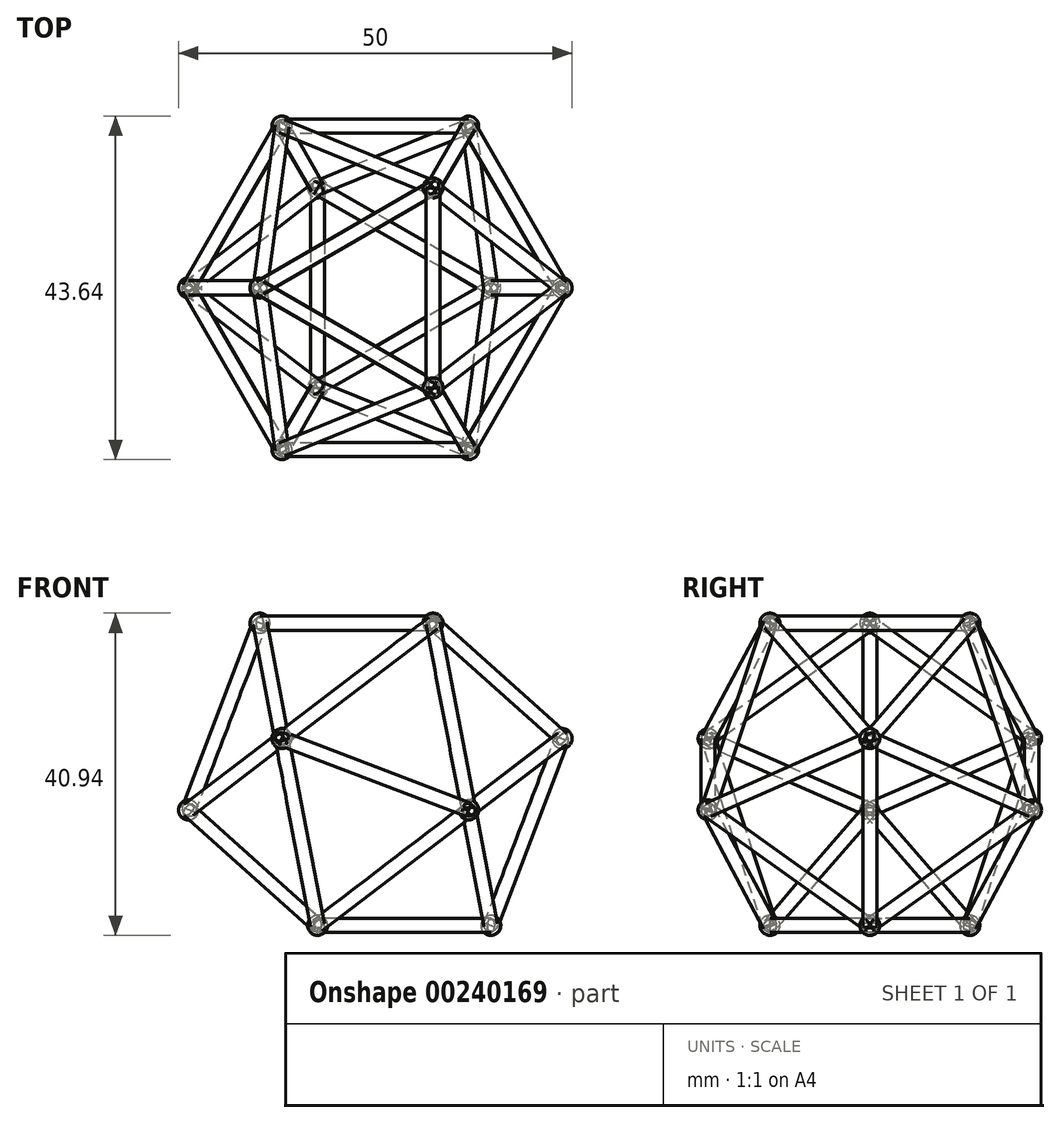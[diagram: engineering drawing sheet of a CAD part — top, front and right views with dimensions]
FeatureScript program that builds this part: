
annotation { "Feature Type Name" : "Feature", "Feature Type Description" : "" }
export const myFeature = defineFeature(function(context is Context, id is Id, definition is map)
    precondition{}
    {
        {
            var Q0;
            Q0=qCreatedBy(makeId("Front.planeOp"),FACE);
            var sketch = newSketch(context, id + "F0", { "sketchPlane" : qUnion([Q0])});
            skLineSegment(sketch, "E0.bottom", {"start": v(-20.55, 12.7) * mm, "end": v(20.55, 12.7) * mm});
            skLineSegment(sketch, "E0.top", {"start": v(-20.55, -12.7) * mm, "end": v(20.55, -12.7) * mm});
            skLineSegment(sketch, "E0.left", {"start": v(-20.55, 12.7) * mm, "end": v(-20.55, -12.7) * mm});
            skLineSegment(sketch, "E0.right", {"start": v(20.55, 12.7) * mm, "end": v(20.55, -12.7) * mm});
            skSolve(sketch);
        }
        {
            var Q0;
            Q0 = qSketchRegion(id + "F0", true);
            extrude(context, id + "F1", {"entities" : qUnion([Q0]), "depth" : 1.27 * mm, "hasSecondDirection" : true, "secondDirectionOppositeDirection" : true, "secondDirectionDepth" : 1.27 * mm});
        }
        {
            var Q0;
            Q0=qCreatedBy(makeId("Top.planeOp"),FACE);
            var sketch = newSketch(context, id + "F2", { "sketchPlane" : qUnion([Q0])});
            skLineSegment(sketch, "E1", {"start": v(0, 0) * mm, "end": v(0, 50.8) * mm});
            skLineSegment(sketch, "E2", {"start": v(0, 0) * mm, "end": v(-50.8, 0) * mm});
            skSolve(sketch);
        }
        {
            var Q0;
            Q0=qCreatedBy(makeId("Front.planeOp"),FACE);
            var sketch = newSketch(context, id + "F3", { "sketchPlane" : qUnion([Q0])});
            skLineSegment(sketch, "E3", {"start": v(0, 0) * mm, "end": v(0, 50.8) * mm});
            skSolve(sketch);
        }
        {
            var Q0;
            Q0=makeQuery(id+"F1.opExtrude","SWEPT_BODY",BODY,{"disambiguationData":[OSD([sQuery(id+"F0.wireOp",EDGE,"E0.bottom"),sQuery(id+"F0.wireOp",EDGE,"E0.top"),sQuery(id+"F0.wireOp",EDGE,"E0.left"),sQuery(id+"F0.wireOp",EDGE,"E0.right")])]});
            var Q1;
            Q1=sQuery(id+"F2.wireOp",EDGE,"E1");
            transform(context, id + "F4", {"entities" : qUnion([Q0]), "transformType" : TransformType.ROTATION, "transformAxis" : qUnion([Q1]), "angle" : 90 * degree, "makeCopy" : true});
        }
        {
            var Q0;
            Q0=makeQuery(id+"F4.opPattern","COPY",BODY,{"derivedFrom":makeQuery(id+"F1.opExtrude","SWEPT_BODY",BODY,{"disambiguationData":[OSD([sQuery(id+"F0.wireOp",EDGE,"E0.bottom"),sQuery(id+"F0.wireOp",EDGE,"E0.top"),sQuery(id+"F0.wireOp",EDGE,"E0.left"),sQuery(id+"F0.wireOp",EDGE,"E0.right")])]}),"instanceName":"1"});
            var Q1;
            Q1=sQuery(id+"F2.wireOp",EDGE,"E2");
            transform(context, id + "F5", {"entities" : qUnion([Q0]), "transformType" : TransformType.ROTATION, "transformAxis" : qUnion([Q1]), "angle" : 90 * degree, "makeCopy" : false});
        }
        {
            var Q0;
            Q0=makeQuery(id+"F1.opExtrude","SWEPT_BODY",BODY,{"disambiguationData":[OSD([sQuery(id+"F0.wireOp",EDGE,"E0.bottom"),sQuery(id+"F0.wireOp",EDGE,"E0.top"),sQuery(id+"F0.wireOp",EDGE,"E0.left"),sQuery(id+"F0.wireOp",EDGE,"E0.right")])]});
            var Q1;
            Q1=sQuery(id+"F3.wireOp",EDGE,"E3");
            transform(context, id + "F6", {"entities" : qUnion([Q0]), "transformType" : TransformType.ROTATION, "transformAxis" : qUnion([Q1]), "angle" : 90 * degree, "makeCopy" : true});
        }
        {
            var Q0;
            Q0=makeQuery(id+"F6.opPattern","COPY",BODY,{"derivedFrom":makeQuery(id+"F1.opExtrude","SWEPT_BODY",BODY,{"disambiguationData":[OSD([sQuery(id+"F0.wireOp",EDGE,"E0.bottom"),sQuery(id+"F0.wireOp",EDGE,"E0.top"),sQuery(id+"F0.wireOp",EDGE,"E0.left"),sQuery(id+"F0.wireOp",EDGE,"E0.right")])]}),"instanceName":"1"});
            var Q1;
            Q1=sQuery(id+"F2.wireOp",EDGE,"E2");
            transform(context, id + "F7", {"entities" : qUnion([Q0]), "transformType" : TransformType.ROTATION, "transformAxis" : qUnion([Q1]), "angle" : 90 * degree, "makeCopy" : false});
        }
        {
            var Q0;
            Q0=makeQuery(id+"F6.opPattern","COPY",FACE,{"derivedFrom":makeQuery(id+"F1.opExtrude","SWEPT_FACE",FACE,{"disambiguationData":[OSD([sQuery(id+"F0.wireOp",EDGE,"E0.left")])]}),"instanceName":"1"});
            var sketch = newSketch(context, id + "F8", { "sketchPlane" : qUnion([Q0])});
            skArc(sketch, "E4", {"start": v(1.27, 12.7) * mm, "mid": v(0, 13.97) * mm, "end": v(-1.27, 12.7) * mm});
            skArc(sketch, "E5", {"start": v(-1.27, -12.7) * mm, "mid": v(0, -13.97) * mm, "end": v(1.27, -12.7) * mm});
            skLineSegment(sketch, "E6", {"start": v(-1.27, 12.7) * mm, "end": v(1.27, 12.7) * mm});
            skLineSegment(sketch, "E7", {"start": v(-1.27, -12.7) * mm, "end": v(1.27, -12.7) * mm});
            skSolve(sketch);
        }
        {
            var Q0;
            Q0=makeQuery(id+"F8.imprint","IMPRINT",FACE,{"disambiguationData":[TD([[makeQuery(id+"F8.imprint","IMPRINT",EDGE,{"derivedFrom":sQuery(id+"F8.wireOp",EDGE,"E4")}),1.0]])]});
            var Q1;
            Q1=sQuery(id+"F8.wireOp",EDGE,"E6");
            revolve(context, id + "F9", {"entities" : qUnion([Q0]), "axis" : qUnion([Q1]), "revolveType" : RevolveType.FULL});
        }
        {
            var Q0;
            Q0=makeQuery(id+"F8.imprint","IMPRINT",FACE,{"disambiguationData":[TD([[makeQuery(id+"F8.imprint","IMPRINT",EDGE,{"derivedFrom":sQuery(id+"F8.wireOp",EDGE,"E5")}),1.0]])]});
            var Q1;
            Q1=sQuery(id+"F8.wireOp",EDGE,"E7");
            revolve(context, id + "F10", {"entities" : qUnion([Q0]), "axis" : qUnion([Q1]), "revolveType" : RevolveType.FULL});
        }
        {
            var Q0;
            Q0=makeQuery(id+"F1.opExtrude","SWEPT_FACE",FACE,{"disambiguationData":[OSD([sQuery(id+"F0.wireOp",EDGE,"E0.right")])]});
            var sketch = newSketch(context, id + "F11", { "sketchPlane" : qUnion([Q0])});
            skArc(sketch, "E8", {"start": v(1.27, 12.7) * mm, "mid": v(0, 13.97) * mm, "end": v(-1.27, 12.7) * mm});
            skArc(sketch, "E9", {"start": v(-1.27, -12.7) * mm, "mid": v(0, -13.97) * mm, "end": v(1.27, -12.7) * mm});
            skLineSegment(sketch, "E10", {"start": v(-1.27, 12.7) * mm, "end": v(1.27, 12.7) * mm});
            skLineSegment(sketch, "E11", {"start": v(-1.27, -12.7) * mm, "end": v(1.27, -12.7) * mm});
            skSolve(sketch);
        }
        {
            var Q0;
            Q0=makeQuery(id+"F11.imprint","IMPRINT",FACE,{"disambiguationData":[TD([[makeQuery(id+"F11.imprint","IMPRINT",EDGE,{"derivedFrom":sQuery(id+"F11.wireOp",EDGE,"E8")}),1.0]])]});
            var Q1;
            Q1=sQuery(id+"F11.wireOp",EDGE,"E10");
            revolve(context, id + "F12", {"entities" : qUnion([Q0]), "axis" : qUnion([Q1]), "revolveType" : RevolveType.FULL});
        }
        {
            var Q0;
            Q0=sQuery(id+"F8.wireOp",EDGE,"E7");
            cPoint(context, id + "F13", {"entities" : qUnion([Q0]), "parameter" : 0.5});
        }
        {
            var Q0;
            Q0=sQuery(id+"F11.wireOp",EDGE,"E10");
            cPoint(context, id + "F14", {"entities" : qUnion([Q0]), "parameter" : 0.5});
        }
        {
            var Q0;
            Q0 = qCreatedBy(id + "F13" ,VERTEX);
            var Q1;
            Q1=sQuery(id+"F8.wireOp",VERTEX,"E4.center");
            var Q2;
            Q2 = qCreatedBy(id + "F14" ,VERTEX);
            cPlane(context, id + "F15", {"entities" : qUnion([Q0, Q1, Q2]), "cplaneType" : CPlaneType.THREE_POINT, "offset" : 25.4 * mm, "width" : 152.4 * mm, "height" : 152.4 * mm});
        }
        {
            var Q0;
            Q0=qCreatedBy(id+"F15.planeOp",FACE);
            var sketch = newSketch(context, id + "F16", { "sketchPlane" : qUnion([Q0])});
            skPoint(sketch, "E12.0", {"position": v(-7.33, 12.7) * mm});
            skPoint(sketch, "E13.0", {"position": v(-7.33, -12.7) * mm});
            skPoint(sketch, "E14.0", {"position": v(14.66, 0) * mm});
            skLineSegment(sketch, "E15", {"start": v(-7.33, 12.7) * mm, "end": v(-7.33, -12.7) * mm});
            skLineSegment(sketch, "E16", {"start": v(-7.33, -12.7) * mm, "end": v(14.66, 0) * mm});
            skLineSegment(sketch, "E17", {"start": v(-7.33, 12.7) * mm, "end": v(14.66, 0) * mm});
            skSolve(sketch);
        }
        {
            var Q0;
            Q0=sQuery(id+"F8.wireOp",EDGE,"E6");
            cPoint(context, id + "F17", {"entities" : qUnion([Q0]), "parameter" : 0.5});
        }
        {
            var Q0;
            Q0 = qCreatedBy(id + "F17" ,VERTEX);
            var Q1;
            Q1=sQuery(id+"F16.wireOp",EDGE,"E17");
            cPlane(context, id + "F18", {"entities" : qUnion([Q0, Q1]), "cplaneType" : CPlaneType.LINE_POINT, "offset" : 25.4 * mm, "width" : 152.4 * mm, "height" : 152.4 * mm});
        }
        {
            var Q0;
            Q0=qCreatedBy(id+"F18.planeOp",FACE);
            var sketch = newSketch(context, id + "F19", { "sketchPlane" : qUnion([Q0])});
            skPoint(sketch, "E18.0", {"position": v(7.33, 19.2) * mm});
            skCircle(sketch, "E19", {"center": v(7.33, 19.2) * mm, "radius": 0.9 * mm});
            skSolve(sketch);
        }
        {
            var Q0;
            Q0 = qSketchRegion(id + "F19", true);
            extrude(context, id + "F20", {"entities" : qUnion([Q0]), "depth" : 25.4 * mm});
        }
        {
            var Q0;
            Q0=sQuery(id+"F8.wireOp",EDGE,"E7");
            cPoint(context, id + "F21", {"entities" : qUnion([Q0]), "parameter" : 0.5});
        }
        {
            var Q0;
            Q0 = qCreatedBy(id + "F21" ,VERTEX);
            var Q1;
            Q1=sQuery(id+"F16.wireOp",EDGE,"E16");
            cPlane(context, id + "F22", {"entities" : qUnion([Q0, Q1]), "cplaneType" : CPlaneType.LINE_POINT, "offset" : 25.4 * mm, "width" : 152.4 * mm, "height" : 152.4 * mm});
        }
        {
            var Q0;
            Q0=qCreatedBy(id+"F22.planeOp",FACE);
            var sketch = newSketch(context, id + "F23", { "sketchPlane" : qUnion([Q0])});
            skPoint(sketch, "E20.0", {"position": v(-7.33, 19.2) * mm});
            skCircle(sketch, "E21", {"center": v(-7.33, 19.2) * mm, "radius": 0.9 * mm});
            skSolve(sketch);
        }
        {
            var Q0;
            Q0 = qSketchRegion(id + "F23", true);
            extrude(context, id + "F24", {"entities" : qUnion([Q0]), "depth" : 25.4 * mm});
        }
        {
            var Q0;
            Q0=makeQuery(id+"F20.opExtrude","SWEPT_BODY",BODY,{"disambiguationData":[OSD([sQuery(id+"F19.wireOp",EDGE,"E19")])]});
            var Q1;
            Q1=makeQuery(id+"F24.opExtrude","SWEPT_BODY",BODY,{"disambiguationData":[OSD([sQuery(id+"F23.wireOp",EDGE,"E21")])]});
            var Q2;
            Q2=makeQuery(id+"F12.opRevolve","SWEPT_BODY",BODY,{"disambiguationData":[OSD([sQuery(id+"F11.wireOp",EDGE,"E8"),sQuery(id+"F11.wireOp",EDGE,"E10")])]});
            var Q3;
            Q3=qCreatedBy(makeId("Right.planeOp"),FACE);
            mirror(context, id + "F25", {"entities" : qUnion([Q0, Q1, Q2]), "mirrorPlane" : qUnion([Q3])});
        }
        {
            var Q0;
            Q0=makeQuery(id+"F25.opPattern","COPY",BODY,{"derivedFrom":makeQuery(id+"F12.opRevolve","SWEPT_BODY",BODY,{"disambiguationData":[OSD([sQuery(id+"F11.wireOp",EDGE,"E8"),sQuery(id+"F11.wireOp",EDGE,"E10")])]}),"instanceName":"1"});
            var Q1;
            Q1=makeQuery(id+"F25.opPattern","COPY",BODY,{"derivedFrom":makeQuery(id+"F20.opExtrude","SWEPT_BODY",BODY,{"disambiguationData":[OSD([sQuery(id+"F19.wireOp",EDGE,"E19")])]}),"instanceName":"1"});
            var Q2;
            Q2=makeQuery(id+"F9.opRevolve","SWEPT_BODY",BODY,{"disambiguationData":[OSD([sQuery(id+"F8.wireOp",EDGE,"E4"),sQuery(id+"F8.wireOp",EDGE,"E6")])]});
            var Q3;
            Q3=makeQuery(id+"F20.opExtrude","SWEPT_BODY",BODY,{"disambiguationData":[OSD([sQuery(id+"F19.wireOp",EDGE,"E19")])]});
            var Q4;
            Q4=makeQuery(id+"F12.opRevolve","SWEPT_BODY",BODY,{"disambiguationData":[OSD([sQuery(id+"F11.wireOp",EDGE,"E8"),sQuery(id+"F11.wireOp",EDGE,"E10")])]});
            var Q5;
            Q5=makeQuery(id+"F10.opRevolve","SWEPT_BODY",BODY,{"disambiguationData":[OSD([sQuery(id+"F8.wireOp",EDGE,"E5"),sQuery(id+"F8.wireOp",EDGE,"E7")])]});
            var Q6;
            Q6=makeQuery(id+"F25.opPattern","COPY",BODY,{"derivedFrom":makeQuery(id+"F24.opExtrude","SWEPT_BODY",BODY,{"disambiguationData":[OSD([sQuery(id+"F23.wireOp",EDGE,"E21")])]}),"instanceName":"1"});
            var Q7;
            Q7=makeQuery(id+"F24.opExtrude","SWEPT_BODY",BODY,{"disambiguationData":[OSD([sQuery(id+"F23.wireOp",EDGE,"E21")])]});
            var Q8;
            Q8=qCreatedBy(makeId("Top.planeOp"),FACE);
            mirror(context, id + "F26", {"entities" : qUnion([Q0, Q1, Q2, Q3, Q4, Q5, Q6, Q7]), "mirrorPlane" : qUnion([Q8])});
        }
        {
            var Q0;
            Q0=makeQuery(id+"F6.opPattern","COPY",FACE,{"derivedFrom":makeQuery(id+"F1.opExtrude","SWEPT_FACE",FACE,{"disambiguationData":[OSD([sQuery(id+"F0.wireOp",EDGE,"E0.top")])]}),"instanceName":"1"});
            var sketch = newSketch(context, id + "F27", { "sketchPlane" : qUnion([Q0])});
            skPoint(sketch, "E22.0", {"position": v(0, 20.55) * mm});
            skCircle(sketch, "E23", {"center": v(0, 20.55) * mm, "radius": 0.9 * mm});
            skSolve(sketch);
        }
        {
            var Q0;
            Q0 = qSketchRegion(id + "F27", true);
            extrude(context, id + "F28", {"entities" : qUnion([Q0]), "oppositeDirection" : true, "depth" : 25.4 * mm});
        }
        {
            var Q0;
            Q0=makeQuery(id+"F28.opExtrude","SWEPT_BODY",BODY,{"disambiguationData":[OSD([sQuery(id+"F27.wireOp",EDGE,"E23")])]});
            var Q1;
            Q1=qCreatedBy(makeId("Top.planeOp"),FACE);
            mirror(context, id + "F29", {"entities" : qUnion([Q0]), "mirrorPlane" : qUnion([Q1])});
        }
        {
            var Q0;
            Q0=makeQuery(id+"F1.opExtrude","SWEPT_BODY",BODY,{"disambiguationData":[OSD([sQuery(id+"F0.wireOp",EDGE,"E0.bottom"),sQuery(id+"F0.wireOp",EDGE,"E0.top"),sQuery(id+"F0.wireOp",EDGE,"E0.left"),sQuery(id+"F0.wireOp",EDGE,"E0.right")])]});
            deleteBodies(context, id + "F30", {"entities" : qUnion([Q0])});
        }
        {
            var Q0;
            Q0=makeQuery(id+"F4.opPattern","COPY",BODY,{"derivedFrom":makeQuery(id+"F1.opExtrude","SWEPT_BODY",BODY,{"disambiguationData":[OSD([sQuery(id+"F0.wireOp",EDGE,"E0.bottom"),sQuery(id+"F0.wireOp",EDGE,"E0.top"),sQuery(id+"F0.wireOp",EDGE,"E0.left"),sQuery(id+"F0.wireOp",EDGE,"E0.right")])]}),"instanceName":"1"});
            deleteBodies(context, id + "F31", {"entities" : qUnion([Q0])});
        }
        {
            var Q0;
            Q0=makeQuery(id+"F6.opPattern","COPY",BODY,{"derivedFrom":makeQuery(id+"F1.opExtrude","SWEPT_BODY",BODY,{"disambiguationData":[OSD([sQuery(id+"F0.wireOp",EDGE,"E0.bottom"),sQuery(id+"F0.wireOp",EDGE,"E0.top"),sQuery(id+"F0.wireOp",EDGE,"E0.left"),sQuery(id+"F0.wireOp",EDGE,"E0.right")])]}),"instanceName":"1"});
            var Q1;
            Q1=makeQuery(id+"F9.opRevolve","SWEPT_BODY",BODY,{"disambiguationData":[OSD([sQuery(id+"F8.wireOp",EDGE,"E4"),sQuery(id+"F8.wireOp",EDGE,"E6")])]});
            var Q2;
            Q2=makeQuery(id+"F10.opRevolve","SWEPT_BODY",BODY,{"disambiguationData":[OSD([sQuery(id+"F8.wireOp",EDGE,"E5"),sQuery(id+"F8.wireOp",EDGE,"E7")])]});
            var Q3;
            Q3=makeQuery(id+"F12.opRevolve","SWEPT_BODY",BODY,{"disambiguationData":[OSD([sQuery(id+"F11.wireOp",EDGE,"E8"),sQuery(id+"F11.wireOp",EDGE,"E10")])]});
            var Q4;
            Q4=makeQuery(id+"F20.opExtrude","SWEPT_BODY",BODY,{"disambiguationData":[OSD([sQuery(id+"F19.wireOp",EDGE,"E19")])]});
            var Q5;
            Q5=makeQuery(id+"F24.opExtrude","SWEPT_BODY",BODY,{"disambiguationData":[OSD([sQuery(id+"F23.wireOp",EDGE,"E21")])]});
            var Q6;
            Q6=makeQuery(id+"F25.opPattern","COPY",BODY,{"derivedFrom":makeQuery(id+"F12.opRevolve","SWEPT_BODY",BODY,{"disambiguationData":[OSD([sQuery(id+"F11.wireOp",EDGE,"E8"),sQuery(id+"F11.wireOp",EDGE,"E10")])]}),"instanceName":"1"});
            var Q7;
            Q7=makeQuery(id+"F25.opPattern","COPY",BODY,{"derivedFrom":makeQuery(id+"F20.opExtrude","SWEPT_BODY",BODY,{"disambiguationData":[OSD([sQuery(id+"F19.wireOp",EDGE,"E19")])]}),"instanceName":"1"});
            var Q8;
            Q8=makeQuery(id+"F25.opPattern","COPY",BODY,{"derivedFrom":makeQuery(id+"F24.opExtrude","SWEPT_BODY",BODY,{"disambiguationData":[OSD([sQuery(id+"F23.wireOp",EDGE,"E21")])]}),"instanceName":"1"});
            var Q9;
            Q9=makeQuery(id+"F26.opPattern","COPY",BODY,{"derivedFrom":makeQuery(id+"F9.opRevolve","SWEPT_BODY",BODY,{"disambiguationData":[OSD([sQuery(id+"F8.wireOp",EDGE,"E4"),sQuery(id+"F8.wireOp",EDGE,"E6")])]}),"instanceName":"1"});
            var Q10;
            Q10=makeQuery(id+"F26.opPattern","COPY",BODY,{"derivedFrom":makeQuery(id+"F10.opRevolve","SWEPT_BODY",BODY,{"disambiguationData":[OSD([sQuery(id+"F8.wireOp",EDGE,"E5"),sQuery(id+"F8.wireOp",EDGE,"E7")])]}),"instanceName":"1"});
            var Q11;
            Q11=makeQuery(id+"F26.opPattern","COPY",BODY,{"derivedFrom":makeQuery(id+"F12.opRevolve","SWEPT_BODY",BODY,{"disambiguationData":[OSD([sQuery(id+"F11.wireOp",EDGE,"E8"),sQuery(id+"F11.wireOp",EDGE,"E10")])]}),"instanceName":"1"});
            var Q12;
            Q12=makeQuery(id+"F26.opPattern","COPY",BODY,{"derivedFrom":makeQuery(id+"F20.opExtrude","SWEPT_BODY",BODY,{"disambiguationData":[OSD([sQuery(id+"F19.wireOp",EDGE,"E19")])]}),"instanceName":"1"});
            var Q13;
            Q13=makeQuery(id+"F26.opPattern","COPY",BODY,{"derivedFrom":makeQuery(id+"F24.opExtrude","SWEPT_BODY",BODY,{"disambiguationData":[OSD([sQuery(id+"F23.wireOp",EDGE,"E21")])]}),"instanceName":"1"});
            var Q14;
            Q14=makeQuery(id+"F26.opPattern","COPY",BODY,{"derivedFrom":makeQuery(id+"F25.opPattern","COPY",BODY,{"derivedFrom":makeQuery(id+"F12.opRevolve","SWEPT_BODY",BODY,{"disambiguationData":[OSD([sQuery(id+"F11.wireOp",EDGE,"E8"),sQuery(id+"F11.wireOp",EDGE,"E10")])]}),"instanceName":"1"}),"instanceName":"1"});
            var Q15;
            Q15=makeQuery(id+"F26.opPattern","COPY",BODY,{"derivedFrom":makeQuery(id+"F25.opPattern","COPY",BODY,{"derivedFrom":makeQuery(id+"F20.opExtrude","SWEPT_BODY",BODY,{"disambiguationData":[OSD([sQuery(id+"F19.wireOp",EDGE,"E19")])]}),"instanceName":"1"}),"instanceName":"1"});
            var Q16;
            Q16=makeQuery(id+"F26.opPattern","COPY",BODY,{"derivedFrom":makeQuery(id+"F25.opPattern","COPY",BODY,{"derivedFrom":makeQuery(id+"F24.opExtrude","SWEPT_BODY",BODY,{"disambiguationData":[OSD([sQuery(id+"F23.wireOp",EDGE,"E21")])]}),"instanceName":"1"}),"instanceName":"1"});
            var Q17;
            Q17=makeQuery(id+"F28.opExtrude","SWEPT_BODY",BODY,{"disambiguationData":[OSD([sQuery(id+"F27.wireOp",EDGE,"E23")])]});
            var Q18;
            Q18=makeQuery(id+"F29.opPattern","COPY",BODY,{"derivedFrom":makeQuery(id+"F28.opExtrude","SWEPT_BODY",BODY,{"disambiguationData":[OSD([sQuery(id+"F27.wireOp",EDGE,"E23")])]}),"instanceName":"1"});
            var Q19;
            Q19=sQuery(id+"F2.wireOp",EDGE,"E1");
            transform(context, id + "F32", {"entities" : qUnion([Q0, Q1, Q2, Q3, Q4, Q5, Q6, Q7, Q8, Q9, Q10, Q11, Q12, Q13, Q14, Q15, Q16, Q17, Q18]), "transformType" : TransformType.ROTATION, "transformAxis" : qUnion([Q19]), "angle" : 90 * degree, "makeCopy" : true});
        }
        {
            var Q0;
            Q0=makeQuery(id+"F32.opPattern","COPY",BODY,{"derivedFrom":makeQuery(id+"F6.opPattern","COPY",BODY,{"derivedFrom":makeQuery(id+"F1.opExtrude","SWEPT_BODY",BODY,{"disambiguationData":[OSD([sQuery(id+"F0.wireOp",EDGE,"E0.bottom"),sQuery(id+"F0.wireOp",EDGE,"E0.top"),sQuery(id+"F0.wireOp",EDGE,"E0.left"),sQuery(id+"F0.wireOp",EDGE,"E0.right")])]}),"instanceName":"1"}),"instanceName":"1"});
            var Q1;
            Q1=makeQuery(id+"F32.opPattern","COPY",BODY,{"derivedFrom":makeQuery(id+"F9.opRevolve","SWEPT_BODY",BODY,{"disambiguationData":[OSD([sQuery(id+"F8.wireOp",EDGE,"E4"),sQuery(id+"F8.wireOp",EDGE,"E6")])]}),"instanceName":"1"});
            var Q2;
            Q2=makeQuery(id+"F32.opPattern","COPY",BODY,{"derivedFrom":makeQuery(id+"F10.opRevolve","SWEPT_BODY",BODY,{"disambiguationData":[OSD([sQuery(id+"F8.wireOp",EDGE,"E5"),sQuery(id+"F8.wireOp",EDGE,"E7")])]}),"instanceName":"1"});
            var Q3;
            Q3=makeQuery(id+"F32.opPattern","COPY",BODY,{"derivedFrom":makeQuery(id+"F12.opRevolve","SWEPT_BODY",BODY,{"disambiguationData":[OSD([sQuery(id+"F11.wireOp",EDGE,"E8"),sQuery(id+"F11.wireOp",EDGE,"E10")])]}),"instanceName":"1"});
            var Q4;
            Q4=makeQuery(id+"F32.opPattern","COPY",BODY,{"derivedFrom":makeQuery(id+"F20.opExtrude","SWEPT_BODY",BODY,{"disambiguationData":[OSD([sQuery(id+"F19.wireOp",EDGE,"E19")])]}),"instanceName":"1"});
            var Q5;
            Q5=makeQuery(id+"F32.opPattern","COPY",BODY,{"derivedFrom":makeQuery(id+"F24.opExtrude","SWEPT_BODY",BODY,{"disambiguationData":[OSD([sQuery(id+"F23.wireOp",EDGE,"E21")])]}),"instanceName":"1"});
            var Q6;
            Q6=makeQuery(id+"F32.opPattern","COPY",BODY,{"derivedFrom":makeQuery(id+"F25.opPattern","COPY",BODY,{"derivedFrom":makeQuery(id+"F12.opRevolve","SWEPT_BODY",BODY,{"disambiguationData":[OSD([sQuery(id+"F11.wireOp",EDGE,"E8"),sQuery(id+"F11.wireOp",EDGE,"E10")])]}),"instanceName":"1"}),"instanceName":"1"});
            var Q7;
            Q7=makeQuery(id+"F32.opPattern","COPY",BODY,{"derivedFrom":makeQuery(id+"F25.opPattern","COPY",BODY,{"derivedFrom":makeQuery(id+"F20.opExtrude","SWEPT_BODY",BODY,{"disambiguationData":[OSD([sQuery(id+"F19.wireOp",EDGE,"E19")])]}),"instanceName":"1"}),"instanceName":"1"});
            var Q8;
            Q8=makeQuery(id+"F32.opPattern","COPY",BODY,{"derivedFrom":makeQuery(id+"F25.opPattern","COPY",BODY,{"derivedFrom":makeQuery(id+"F24.opExtrude","SWEPT_BODY",BODY,{"disambiguationData":[OSD([sQuery(id+"F23.wireOp",EDGE,"E21")])]}),"instanceName":"1"}),"instanceName":"1"});
            var Q9;
            Q9=makeQuery(id+"F32.opPattern","COPY",BODY,{"derivedFrom":makeQuery(id+"F26.opPattern","COPY",BODY,{"derivedFrom":makeQuery(id+"F9.opRevolve","SWEPT_BODY",BODY,{"disambiguationData":[OSD([sQuery(id+"F8.wireOp",EDGE,"E4"),sQuery(id+"F8.wireOp",EDGE,"E6")])]}),"instanceName":"1"}),"instanceName":"1"});
            var Q10;
            Q10=makeQuery(id+"F32.opPattern","COPY",BODY,{"derivedFrom":makeQuery(id+"F26.opPattern","COPY",BODY,{"derivedFrom":makeQuery(id+"F10.opRevolve","SWEPT_BODY",BODY,{"disambiguationData":[OSD([sQuery(id+"F8.wireOp",EDGE,"E5"),sQuery(id+"F8.wireOp",EDGE,"E7")])]}),"instanceName":"1"}),"instanceName":"1"});
            var Q11;
            Q11=makeQuery(id+"F32.opPattern","COPY",BODY,{"derivedFrom":makeQuery(id+"F26.opPattern","COPY",BODY,{"derivedFrom":makeQuery(id+"F12.opRevolve","SWEPT_BODY",BODY,{"disambiguationData":[OSD([sQuery(id+"F11.wireOp",EDGE,"E8"),sQuery(id+"F11.wireOp",EDGE,"E10")])]}),"instanceName":"1"}),"instanceName":"1"});
            var Q12;
            Q12=makeQuery(id+"F32.opPattern","COPY",BODY,{"derivedFrom":makeQuery(id+"F26.opPattern","COPY",BODY,{"derivedFrom":makeQuery(id+"F20.opExtrude","SWEPT_BODY",BODY,{"disambiguationData":[OSD([sQuery(id+"F19.wireOp",EDGE,"E19")])]}),"instanceName":"1"}),"instanceName":"1"});
            var Q13;
            Q13=makeQuery(id+"F32.opPattern","COPY",BODY,{"derivedFrom":makeQuery(id+"F26.opPattern","COPY",BODY,{"derivedFrom":makeQuery(id+"F24.opExtrude","SWEPT_BODY",BODY,{"disambiguationData":[OSD([sQuery(id+"F23.wireOp",EDGE,"E21")])]}),"instanceName":"1"}),"instanceName":"1"});
            var Q14;
            Q14=makeQuery(id+"F32.opPattern","COPY",BODY,{"derivedFrom":makeQuery(id+"F26.opPattern","COPY",BODY,{"derivedFrom":makeQuery(id+"F25.opPattern","COPY",BODY,{"derivedFrom":makeQuery(id+"F12.opRevolve","SWEPT_BODY",BODY,{"disambiguationData":[OSD([sQuery(id+"F11.wireOp",EDGE,"E8"),sQuery(id+"F11.wireOp",EDGE,"E10")])]}),"instanceName":"1"}),"instanceName":"1"}),"instanceName":"1"});
            var Q15;
            Q15=makeQuery(id+"F32.opPattern","COPY",BODY,{"derivedFrom":makeQuery(id+"F26.opPattern","COPY",BODY,{"derivedFrom":makeQuery(id+"F25.opPattern","COPY",BODY,{"derivedFrom":makeQuery(id+"F20.opExtrude","SWEPT_BODY",BODY,{"disambiguationData":[OSD([sQuery(id+"F19.wireOp",EDGE,"E19")])]}),"instanceName":"1"}),"instanceName":"1"}),"instanceName":"1"});
            var Q16;
            Q16=makeQuery(id+"F32.opPattern","COPY",BODY,{"derivedFrom":makeQuery(id+"F26.opPattern","COPY",BODY,{"derivedFrom":makeQuery(id+"F25.opPattern","COPY",BODY,{"derivedFrom":makeQuery(id+"F24.opExtrude","SWEPT_BODY",BODY,{"disambiguationData":[OSD([sQuery(id+"F23.wireOp",EDGE,"E21")])]}),"instanceName":"1"}),"instanceName":"1"}),"instanceName":"1"});
            var Q17;
            Q17=makeQuery(id+"F32.opPattern","COPY",BODY,{"derivedFrom":makeQuery(id+"F28.opExtrude","SWEPT_BODY",BODY,{"disambiguationData":[OSD([sQuery(id+"F27.wireOp",EDGE,"E23")])]}),"instanceName":"1"});
            var Q18;
            Q18=makeQuery(id+"F32.opPattern","COPY",BODY,{"derivedFrom":makeQuery(id+"F29.opPattern","COPY",BODY,{"derivedFrom":makeQuery(id+"F28.opExtrude","SWEPT_BODY",BODY,{"disambiguationData":[OSD([sQuery(id+"F27.wireOp",EDGE,"E23")])]}),"instanceName":"1"}),"instanceName":"1"});
            var Q19;
            Q19=sQuery(id+"F3.wireOp",EDGE,"E3");
            transform(context, id + "F33", {"entities" : qUnion([Q0, Q1, Q2, Q3, Q4, Q5, Q6, Q7, Q8, Q9, Q10, Q11, Q12, Q13, Q14, Q15, Q16, Q17, Q18]), "transformType" : TransformType.ROTATION, "transformAxis" : qUnion([Q19]), "angle" : 90 * degree, "makeCopy" : false});
        }
        {
            var Q0;
            Q0=makeQuery(id+"F6.opPattern","COPY",BODY,{"derivedFrom":makeQuery(id+"F1.opExtrude","SWEPT_BODY",BODY,{"disambiguationData":[OSD([sQuery(id+"F0.wireOp",EDGE,"E0.bottom"),sQuery(id+"F0.wireOp",EDGE,"E0.top"),sQuery(id+"F0.wireOp",EDGE,"E0.left"),sQuery(id+"F0.wireOp",EDGE,"E0.right")])]}),"instanceName":"1"});
            var Q1;
            Q1=makeQuery(id+"F9.opRevolve","SWEPT_BODY",BODY,{"disambiguationData":[OSD([sQuery(id+"F8.wireOp",EDGE,"E4"),sQuery(id+"F8.wireOp",EDGE,"E6")])]});
            var Q2;
            Q2=makeQuery(id+"F10.opRevolve","SWEPT_BODY",BODY,{"disambiguationData":[OSD([sQuery(id+"F8.wireOp",EDGE,"E5"),sQuery(id+"F8.wireOp",EDGE,"E7")])]});
            var Q3;
            Q3=makeQuery(id+"F12.opRevolve","SWEPT_BODY",BODY,{"disambiguationData":[OSD([sQuery(id+"F11.wireOp",EDGE,"E8"),sQuery(id+"F11.wireOp",EDGE,"E10")])]});
            var Q4;
            Q4=makeQuery(id+"F20.opExtrude","SWEPT_BODY",BODY,{"disambiguationData":[OSD([sQuery(id+"F19.wireOp",EDGE,"E19")])]});
            var Q5;
            Q5=makeQuery(id+"F24.opExtrude","SWEPT_BODY",BODY,{"disambiguationData":[OSD([sQuery(id+"F23.wireOp",EDGE,"E21")])]});
            var Q6;
            Q6=makeQuery(id+"F25.opPattern","COPY",BODY,{"derivedFrom":makeQuery(id+"F12.opRevolve","SWEPT_BODY",BODY,{"disambiguationData":[OSD([sQuery(id+"F11.wireOp",EDGE,"E8"),sQuery(id+"F11.wireOp",EDGE,"E10")])]}),"instanceName":"1"});
            var Q7;
            Q7=makeQuery(id+"F25.opPattern","COPY",BODY,{"derivedFrom":makeQuery(id+"F20.opExtrude","SWEPT_BODY",BODY,{"disambiguationData":[OSD([sQuery(id+"F19.wireOp",EDGE,"E19")])]}),"instanceName":"1"});
            var Q8;
            Q8=makeQuery(id+"F25.opPattern","COPY",BODY,{"derivedFrom":makeQuery(id+"F24.opExtrude","SWEPT_BODY",BODY,{"disambiguationData":[OSD([sQuery(id+"F23.wireOp",EDGE,"E21")])]}),"instanceName":"1"});
            var Q9;
            Q9=makeQuery(id+"F26.opPattern","COPY",BODY,{"derivedFrom":makeQuery(id+"F9.opRevolve","SWEPT_BODY",BODY,{"disambiguationData":[OSD([sQuery(id+"F8.wireOp",EDGE,"E4"),sQuery(id+"F8.wireOp",EDGE,"E6")])]}),"instanceName":"1"});
            var Q10;
            Q10=makeQuery(id+"F26.opPattern","COPY",BODY,{"derivedFrom":makeQuery(id+"F10.opRevolve","SWEPT_BODY",BODY,{"disambiguationData":[OSD([sQuery(id+"F8.wireOp",EDGE,"E5"),sQuery(id+"F8.wireOp",EDGE,"E7")])]}),"instanceName":"1"});
            var Q11;
            Q11=makeQuery(id+"F26.opPattern","COPY",BODY,{"derivedFrom":makeQuery(id+"F12.opRevolve","SWEPT_BODY",BODY,{"disambiguationData":[OSD([sQuery(id+"F11.wireOp",EDGE,"E8"),sQuery(id+"F11.wireOp",EDGE,"E10")])]}),"instanceName":"1"});
            var Q12;
            Q12=makeQuery(id+"F26.opPattern","COPY",BODY,{"derivedFrom":makeQuery(id+"F20.opExtrude","SWEPT_BODY",BODY,{"disambiguationData":[OSD([sQuery(id+"F19.wireOp",EDGE,"E19")])]}),"instanceName":"1"});
            var Q13;
            Q13=makeQuery(id+"F26.opPattern","COPY",BODY,{"derivedFrom":makeQuery(id+"F24.opExtrude","SWEPT_BODY",BODY,{"disambiguationData":[OSD([sQuery(id+"F23.wireOp",EDGE,"E21")])]}),"instanceName":"1"});
            var Q14;
            Q14=makeQuery(id+"F26.opPattern","COPY",BODY,{"derivedFrom":makeQuery(id+"F25.opPattern","COPY",BODY,{"derivedFrom":makeQuery(id+"F12.opRevolve","SWEPT_BODY",BODY,{"disambiguationData":[OSD([sQuery(id+"F11.wireOp",EDGE,"E8"),sQuery(id+"F11.wireOp",EDGE,"E10")])]}),"instanceName":"1"}),"instanceName":"1"});
            var Q15;
            Q15=makeQuery(id+"F26.opPattern","COPY",BODY,{"derivedFrom":makeQuery(id+"F25.opPattern","COPY",BODY,{"derivedFrom":makeQuery(id+"F20.opExtrude","SWEPT_BODY",BODY,{"disambiguationData":[OSD([sQuery(id+"F19.wireOp",EDGE,"E19")])]}),"instanceName":"1"}),"instanceName":"1"});
            var Q16;
            Q16=makeQuery(id+"F26.opPattern","COPY",BODY,{"derivedFrom":makeQuery(id+"F25.opPattern","COPY",BODY,{"derivedFrom":makeQuery(id+"F24.opExtrude","SWEPT_BODY",BODY,{"disambiguationData":[OSD([sQuery(id+"F23.wireOp",EDGE,"E21")])]}),"instanceName":"1"}),"instanceName":"1"});
            var Q17;
            Q17=makeQuery(id+"F28.opExtrude","SWEPT_BODY",BODY,{"disambiguationData":[OSD([sQuery(id+"F27.wireOp",EDGE,"E23")])]});
            var Q18;
            Q18=makeQuery(id+"F29.opPattern","COPY",BODY,{"derivedFrom":makeQuery(id+"F28.opExtrude","SWEPT_BODY",BODY,{"disambiguationData":[OSD([sQuery(id+"F27.wireOp",EDGE,"E23")])]}),"instanceName":"1"});
            var Q19;
            Q19=sQuery(id+"F2.wireOp",EDGE,"E1");
            transform(context, id + "F34", {"entities" : qUnion([Q0, Q1, Q2, Q3, Q4, Q5, Q6, Q7, Q8, Q9, Q10, Q11, Q12, Q13, Q14, Q15, Q16, Q17, Q18]), "transformType" : TransformType.ROTATION, "transformAxis" : qUnion([Q19]), "angle" : 90 * degree, "makeCopy" : true});
        }
        {
            var Q0;
            Q0=makeQuery(id+"F34.opPattern","COPY",BODY,{"derivedFrom":makeQuery(id+"F6.opPattern","COPY",BODY,{"derivedFrom":makeQuery(id+"F1.opExtrude","SWEPT_BODY",BODY,{"disambiguationData":[OSD([sQuery(id+"F0.wireOp",EDGE,"E0.bottom"),sQuery(id+"F0.wireOp",EDGE,"E0.top"),sQuery(id+"F0.wireOp",EDGE,"E0.left"),sQuery(id+"F0.wireOp",EDGE,"E0.right")])]}),"instanceName":"1"}),"instanceName":"1"});
            var Q1;
            Q1=makeQuery(id+"F34.opPattern","COPY",BODY,{"derivedFrom":makeQuery(id+"F9.opRevolve","SWEPT_BODY",BODY,{"disambiguationData":[OSD([sQuery(id+"F8.wireOp",EDGE,"E4"),sQuery(id+"F8.wireOp",EDGE,"E6")])]}),"instanceName":"1"});
            var Q2;
            Q2=makeQuery(id+"F34.opPattern","COPY",BODY,{"derivedFrom":makeQuery(id+"F10.opRevolve","SWEPT_BODY",BODY,{"disambiguationData":[OSD([sQuery(id+"F8.wireOp",EDGE,"E5"),sQuery(id+"F8.wireOp",EDGE,"E7")])]}),"instanceName":"1"});
            var Q3;
            Q3=makeQuery(id+"F34.opPattern","COPY",BODY,{"derivedFrom":makeQuery(id+"F12.opRevolve","SWEPT_BODY",BODY,{"disambiguationData":[OSD([sQuery(id+"F11.wireOp",EDGE,"E8"),sQuery(id+"F11.wireOp",EDGE,"E10")])]}),"instanceName":"1"});
            var Q4;
            Q4=makeQuery(id+"F34.opPattern","COPY",BODY,{"derivedFrom":makeQuery(id+"F20.opExtrude","SWEPT_BODY",BODY,{"disambiguationData":[OSD([sQuery(id+"F19.wireOp",EDGE,"E19")])]}),"instanceName":"1"});
            var Q5;
            Q5=makeQuery(id+"F34.opPattern","COPY",BODY,{"derivedFrom":makeQuery(id+"F24.opExtrude","SWEPT_BODY",BODY,{"disambiguationData":[OSD([sQuery(id+"F23.wireOp",EDGE,"E21")])]}),"instanceName":"1"});
            var Q6;
            Q6=makeQuery(id+"F34.opPattern","COPY",BODY,{"derivedFrom":makeQuery(id+"F25.opPattern","COPY",BODY,{"derivedFrom":makeQuery(id+"F12.opRevolve","SWEPT_BODY",BODY,{"disambiguationData":[OSD([sQuery(id+"F11.wireOp",EDGE,"E8"),sQuery(id+"F11.wireOp",EDGE,"E10")])]}),"instanceName":"1"}),"instanceName":"1"});
            var Q7;
            Q7=makeQuery(id+"F34.opPattern","COPY",BODY,{"derivedFrom":makeQuery(id+"F25.opPattern","COPY",BODY,{"derivedFrom":makeQuery(id+"F20.opExtrude","SWEPT_BODY",BODY,{"disambiguationData":[OSD([sQuery(id+"F19.wireOp",EDGE,"E19")])]}),"instanceName":"1"}),"instanceName":"1"});
            var Q8;
            Q8=makeQuery(id+"F34.opPattern","COPY",BODY,{"derivedFrom":makeQuery(id+"F25.opPattern","COPY",BODY,{"derivedFrom":makeQuery(id+"F24.opExtrude","SWEPT_BODY",BODY,{"disambiguationData":[OSD([sQuery(id+"F23.wireOp",EDGE,"E21")])]}),"instanceName":"1"}),"instanceName":"1"});
            var Q9;
            Q9=makeQuery(id+"F34.opPattern","COPY",BODY,{"derivedFrom":makeQuery(id+"F26.opPattern","COPY",BODY,{"derivedFrom":makeQuery(id+"F9.opRevolve","SWEPT_BODY",BODY,{"disambiguationData":[OSD([sQuery(id+"F8.wireOp",EDGE,"E4"),sQuery(id+"F8.wireOp",EDGE,"E6")])]}),"instanceName":"1"}),"instanceName":"1"});
            var Q10;
            Q10=makeQuery(id+"F34.opPattern","COPY",BODY,{"derivedFrom":makeQuery(id+"F26.opPattern","COPY",BODY,{"derivedFrom":makeQuery(id+"F10.opRevolve","SWEPT_BODY",BODY,{"disambiguationData":[OSD([sQuery(id+"F8.wireOp",EDGE,"E5"),sQuery(id+"F8.wireOp",EDGE,"E7")])]}),"instanceName":"1"}),"instanceName":"1"});
            var Q11;
            Q11=makeQuery(id+"F34.opPattern","COPY",BODY,{"derivedFrom":makeQuery(id+"F26.opPattern","COPY",BODY,{"derivedFrom":makeQuery(id+"F12.opRevolve","SWEPT_BODY",BODY,{"disambiguationData":[OSD([sQuery(id+"F11.wireOp",EDGE,"E8"),sQuery(id+"F11.wireOp",EDGE,"E10")])]}),"instanceName":"1"}),"instanceName":"1"});
            var Q12;
            Q12=makeQuery(id+"F34.opPattern","COPY",BODY,{"derivedFrom":makeQuery(id+"F26.opPattern","COPY",BODY,{"derivedFrom":makeQuery(id+"F20.opExtrude","SWEPT_BODY",BODY,{"disambiguationData":[OSD([sQuery(id+"F19.wireOp",EDGE,"E19")])]}),"instanceName":"1"}),"instanceName":"1"});
            var Q13;
            Q13=makeQuery(id+"F34.opPattern","COPY",BODY,{"derivedFrom":makeQuery(id+"F26.opPattern","COPY",BODY,{"derivedFrom":makeQuery(id+"F24.opExtrude","SWEPT_BODY",BODY,{"disambiguationData":[OSD([sQuery(id+"F23.wireOp",EDGE,"E21")])]}),"instanceName":"1"}),"instanceName":"1"});
            var Q14;
            Q14=makeQuery(id+"F34.opPattern","COPY",BODY,{"derivedFrom":makeQuery(id+"F26.opPattern","COPY",BODY,{"derivedFrom":makeQuery(id+"F25.opPattern","COPY",BODY,{"derivedFrom":makeQuery(id+"F12.opRevolve","SWEPT_BODY",BODY,{"disambiguationData":[OSD([sQuery(id+"F11.wireOp",EDGE,"E8"),sQuery(id+"F11.wireOp",EDGE,"E10")])]}),"instanceName":"1"}),"instanceName":"1"}),"instanceName":"1"});
            var Q15;
            Q15=makeQuery(id+"F34.opPattern","COPY",BODY,{"derivedFrom":makeQuery(id+"F26.opPattern","COPY",BODY,{"derivedFrom":makeQuery(id+"F25.opPattern","COPY",BODY,{"derivedFrom":makeQuery(id+"F20.opExtrude","SWEPT_BODY",BODY,{"disambiguationData":[OSD([sQuery(id+"F19.wireOp",EDGE,"E19")])]}),"instanceName":"1"}),"instanceName":"1"}),"instanceName":"1"});
            var Q16;
            Q16=makeQuery(id+"F34.opPattern","COPY",BODY,{"derivedFrom":makeQuery(id+"F26.opPattern","COPY",BODY,{"derivedFrom":makeQuery(id+"F25.opPattern","COPY",BODY,{"derivedFrom":makeQuery(id+"F24.opExtrude","SWEPT_BODY",BODY,{"disambiguationData":[OSD([sQuery(id+"F23.wireOp",EDGE,"E21")])]}),"instanceName":"1"}),"instanceName":"1"}),"instanceName":"1"});
            var Q17;
            Q17=makeQuery(id+"F34.opPattern","COPY",BODY,{"derivedFrom":makeQuery(id+"F28.opExtrude","SWEPT_BODY",BODY,{"disambiguationData":[OSD([sQuery(id+"F27.wireOp",EDGE,"E23")])]}),"instanceName":"1"});
            var Q18;
            Q18=makeQuery(id+"F34.opPattern","COPY",BODY,{"derivedFrom":makeQuery(id+"F29.opPattern","COPY",BODY,{"derivedFrom":makeQuery(id+"F28.opExtrude","SWEPT_BODY",BODY,{"disambiguationData":[OSD([sQuery(id+"F27.wireOp",EDGE,"E23")])]}),"instanceName":"1"}),"instanceName":"1"});
            var Q19;
            Q19=sQuery(id+"F2.wireOp",EDGE,"E2");
            transform(context, id + "F35", {"entities" : qUnion([Q0, Q1, Q2, Q3, Q4, Q5, Q6, Q7, Q8, Q9, Q10, Q11, Q12, Q13, Q14, Q15, Q16, Q17, Q18]), "transformType" : TransformType.ROTATION, "transformAxis" : qUnion([Q19]), "angle" : 90 * degree, "makeCopy" : false});
        }
        {
            var Q0;
            Q0=makeQuery(id+"F9.opRevolve","SWEPT_BODY",BODY,{"disambiguationData":[OSD([sQuery(id+"F8.wireOp",EDGE,"E4"),sQuery(id+"F8.wireOp",EDGE,"E6")])]});
            var Q1;
            Q1=makeQuery(id+"F10.opRevolve","SWEPT_BODY",BODY,{"disambiguationData":[OSD([sQuery(id+"F8.wireOp",EDGE,"E5"),sQuery(id+"F8.wireOp",EDGE,"E7")])]});
            var Q2;
            Q2=makeQuery(id+"F12.opRevolve","SWEPT_BODY",BODY,{"disambiguationData":[OSD([sQuery(id+"F11.wireOp",EDGE,"E8"),sQuery(id+"F11.wireOp",EDGE,"E10")])]});
            var Q3;
            Q3=makeQuery(id+"F20.opExtrude","SWEPT_BODY",BODY,{"disambiguationData":[OSD([sQuery(id+"F19.wireOp",EDGE,"E19")])]});
            var Q4;
            Q4=makeQuery(id+"F24.opExtrude","SWEPT_BODY",BODY,{"disambiguationData":[OSD([sQuery(id+"F23.wireOp",EDGE,"E21")])]});
            var Q5;
            Q5=makeQuery(id+"F25.opPattern","COPY",BODY,{"derivedFrom":makeQuery(id+"F12.opRevolve","SWEPT_BODY",BODY,{"disambiguationData":[OSD([sQuery(id+"F11.wireOp",EDGE,"E8"),sQuery(id+"F11.wireOp",EDGE,"E10")])]}),"instanceName":"1"});
            var Q6;
            Q6=makeQuery(id+"F25.opPattern","COPY",BODY,{"derivedFrom":makeQuery(id+"F20.opExtrude","SWEPT_BODY",BODY,{"disambiguationData":[OSD([sQuery(id+"F19.wireOp",EDGE,"E19")])]}),"instanceName":"1"});
            var Q7;
            Q7=makeQuery(id+"F25.opPattern","COPY",BODY,{"derivedFrom":makeQuery(id+"F24.opExtrude","SWEPT_BODY",BODY,{"disambiguationData":[OSD([sQuery(id+"F23.wireOp",EDGE,"E21")])]}),"instanceName":"1"});
            var Q8;
            Q8=makeQuery(id+"F26.opPattern","COPY",BODY,{"derivedFrom":makeQuery(id+"F12.opRevolve","SWEPT_BODY",BODY,{"disambiguationData":[OSD([sQuery(id+"F11.wireOp",EDGE,"E8"),sQuery(id+"F11.wireOp",EDGE,"E10")])]}),"instanceName":"1"});
            var Q9;
            Q9=makeQuery(id+"F26.opPattern","COPY",BODY,{"derivedFrom":makeQuery(id+"F20.opExtrude","SWEPT_BODY",BODY,{"disambiguationData":[OSD([sQuery(id+"F19.wireOp",EDGE,"E19")])]}),"instanceName":"1"});
            var Q10;
            Q10=makeQuery(id+"F26.opPattern","COPY",BODY,{"derivedFrom":makeQuery(id+"F24.opExtrude","SWEPT_BODY",BODY,{"disambiguationData":[OSD([sQuery(id+"F23.wireOp",EDGE,"E21")])]}),"instanceName":"1"});
            var Q11;
            Q11=makeQuery(id+"F26.opPattern","COPY",BODY,{"derivedFrom":makeQuery(id+"F25.opPattern","COPY",BODY,{"derivedFrom":makeQuery(id+"F12.opRevolve","SWEPT_BODY",BODY,{"disambiguationData":[OSD([sQuery(id+"F11.wireOp",EDGE,"E8"),sQuery(id+"F11.wireOp",EDGE,"E10")])]}),"instanceName":"1"}),"instanceName":"1"});
            var Q12;
            Q12=makeQuery(id+"F26.opPattern","COPY",BODY,{"derivedFrom":makeQuery(id+"F25.opPattern","COPY",BODY,{"derivedFrom":makeQuery(id+"F20.opExtrude","SWEPT_BODY",BODY,{"disambiguationData":[OSD([sQuery(id+"F19.wireOp",EDGE,"E19")])]}),"instanceName":"1"}),"instanceName":"1"});
            var Q13;
            Q13=makeQuery(id+"F26.opPattern","COPY",BODY,{"derivedFrom":makeQuery(id+"F25.opPattern","COPY",BODY,{"derivedFrom":makeQuery(id+"F24.opExtrude","SWEPT_BODY",BODY,{"disambiguationData":[OSD([sQuery(id+"F23.wireOp",EDGE,"E21")])]}),"instanceName":"1"}),"instanceName":"1"});
            var Q14;
            Q14=makeQuery(id+"F28.opExtrude","SWEPT_BODY",BODY,{"disambiguationData":[OSD([sQuery(id+"F27.wireOp",EDGE,"E23")])]});
            var Q15;
            Q15=makeQuery(id+"F29.opPattern","COPY",BODY,{"derivedFrom":makeQuery(id+"F28.opExtrude","SWEPT_BODY",BODY,{"disambiguationData":[OSD([sQuery(id+"F27.wireOp",EDGE,"E23")])]}),"instanceName":"1"});
            var Q16;
            Q16=makeQuery(id+"F32.opPattern","COPY",BODY,{"derivedFrom":makeQuery(id+"F10.opRevolve","SWEPT_BODY",BODY,{"disambiguationData":[OSD([sQuery(id+"F8.wireOp",EDGE,"E5"),sQuery(id+"F8.wireOp",EDGE,"E7")])]}),"instanceName":"1"});
            var Q17;
            Q17=makeQuery(id+"F32.opPattern","COPY",BODY,{"derivedFrom":makeQuery(id+"F20.opExtrude","SWEPT_BODY",BODY,{"disambiguationData":[OSD([sQuery(id+"F19.wireOp",EDGE,"E19")])]}),"instanceName":"1"});
            var Q18;
            Q18=makeQuery(id+"F32.opPattern","COPY",BODY,{"derivedFrom":makeQuery(id+"F24.opExtrude","SWEPT_BODY",BODY,{"disambiguationData":[OSD([sQuery(id+"F23.wireOp",EDGE,"E21")])]}),"instanceName":"1"});
            var Q19;
            Q19=makeQuery(id+"F32.opPattern","COPY",BODY,{"derivedFrom":makeQuery(id+"F25.opPattern","COPY",BODY,{"derivedFrom":makeQuery(id+"F12.opRevolve","SWEPT_BODY",BODY,{"disambiguationData":[OSD([sQuery(id+"F11.wireOp",EDGE,"E8"),sQuery(id+"F11.wireOp",EDGE,"E10")])]}),"instanceName":"1"}),"instanceName":"1"});
            var Q20;
            Q20=makeQuery(id+"F32.opPattern","COPY",BODY,{"derivedFrom":makeQuery(id+"F25.opPattern","COPY",BODY,{"derivedFrom":makeQuery(id+"F20.opExtrude","SWEPT_BODY",BODY,{"disambiguationData":[OSD([sQuery(id+"F19.wireOp",EDGE,"E19")])]}),"instanceName":"1"}),"instanceName":"1"});
            var Q21;
            Q21=makeQuery(id+"F32.opPattern","COPY",BODY,{"derivedFrom":makeQuery(id+"F25.opPattern","COPY",BODY,{"derivedFrom":makeQuery(id+"F24.opExtrude","SWEPT_BODY",BODY,{"disambiguationData":[OSD([sQuery(id+"F23.wireOp",EDGE,"E21")])]}),"instanceName":"1"}),"instanceName":"1"});
            var Q22;
            Q22=makeQuery(id+"F32.opPattern","COPY",BODY,{"derivedFrom":makeQuery(id+"F26.opPattern","COPY",BODY,{"derivedFrom":makeQuery(id+"F10.opRevolve","SWEPT_BODY",BODY,{"disambiguationData":[OSD([sQuery(id+"F8.wireOp",EDGE,"E5"),sQuery(id+"F8.wireOp",EDGE,"E7")])]}),"instanceName":"1"}),"instanceName":"1"});
            var Q23;
            Q23=makeQuery(id+"F32.opPattern","COPY",BODY,{"derivedFrom":makeQuery(id+"F26.opPattern","COPY",BODY,{"derivedFrom":makeQuery(id+"F12.opRevolve","SWEPT_BODY",BODY,{"disambiguationData":[OSD([sQuery(id+"F11.wireOp",EDGE,"E8"),sQuery(id+"F11.wireOp",EDGE,"E10")])]}),"instanceName":"1"}),"instanceName":"1"});
            var Q24;
            Q24=makeQuery(id+"F32.opPattern","COPY",BODY,{"derivedFrom":makeQuery(id+"F26.opPattern","COPY",BODY,{"derivedFrom":makeQuery(id+"F20.opExtrude","SWEPT_BODY",BODY,{"disambiguationData":[OSD([sQuery(id+"F19.wireOp",EDGE,"E19")])]}),"instanceName":"1"}),"instanceName":"1"});
            var Q25;
            Q25=makeQuery(id+"F32.opPattern","COPY",BODY,{"derivedFrom":makeQuery(id+"F26.opPattern","COPY",BODY,{"derivedFrom":makeQuery(id+"F24.opExtrude","SWEPT_BODY",BODY,{"disambiguationData":[OSD([sQuery(id+"F23.wireOp",EDGE,"E21")])]}),"instanceName":"1"}),"instanceName":"1"});
            var Q26;
            Q26=makeQuery(id+"F32.opPattern","COPY",BODY,{"derivedFrom":makeQuery(id+"F26.opPattern","COPY",BODY,{"derivedFrom":makeQuery(id+"F25.opPattern","COPY",BODY,{"derivedFrom":makeQuery(id+"F12.opRevolve","SWEPT_BODY",BODY,{"disambiguationData":[OSD([sQuery(id+"F11.wireOp",EDGE,"E8"),sQuery(id+"F11.wireOp",EDGE,"E10")])]}),"instanceName":"1"}),"instanceName":"1"}),"instanceName":"1"});
            var Q27;
            Q27=makeQuery(id+"F32.opPattern","COPY",BODY,{"derivedFrom":makeQuery(id+"F26.opPattern","COPY",BODY,{"derivedFrom":makeQuery(id+"F25.opPattern","COPY",BODY,{"derivedFrom":makeQuery(id+"F20.opExtrude","SWEPT_BODY",BODY,{"disambiguationData":[OSD([sQuery(id+"F19.wireOp",EDGE,"E19")])]}),"instanceName":"1"}),"instanceName":"1"}),"instanceName":"1"});
            var Q28;
            Q28=makeQuery(id+"F32.opPattern","COPY",BODY,{"derivedFrom":makeQuery(id+"F26.opPattern","COPY",BODY,{"derivedFrom":makeQuery(id+"F25.opPattern","COPY",BODY,{"derivedFrom":makeQuery(id+"F24.opExtrude","SWEPT_BODY",BODY,{"disambiguationData":[OSD([sQuery(id+"F23.wireOp",EDGE,"E21")])]}),"instanceName":"1"}),"instanceName":"1"}),"instanceName":"1"});
            var Q29;
            Q29=makeQuery(id+"F32.opPattern","COPY",BODY,{"derivedFrom":makeQuery(id+"F28.opExtrude","SWEPT_BODY",BODY,{"disambiguationData":[OSD([sQuery(id+"F27.wireOp",EDGE,"E23")])]}),"instanceName":"1"});
            var Q30;
            Q30=makeQuery(id+"F32.opPattern","COPY",BODY,{"derivedFrom":makeQuery(id+"F29.opPattern","COPY",BODY,{"derivedFrom":makeQuery(id+"F28.opExtrude","SWEPT_BODY",BODY,{"disambiguationData":[OSD([sQuery(id+"F27.wireOp",EDGE,"E23")])]}),"instanceName":"1"}),"instanceName":"1"});
            var Q31;
            Q31=makeQuery(id+"F34.opPattern","COPY",BODY,{"derivedFrom":makeQuery(id+"F10.opRevolve","SWEPT_BODY",BODY,{"disambiguationData":[OSD([sQuery(id+"F8.wireOp",EDGE,"E5"),sQuery(id+"F8.wireOp",EDGE,"E7")])]}),"instanceName":"1"});
            var Q32;
            Q32=makeQuery(id+"F34.opPattern","COPY",BODY,{"derivedFrom":makeQuery(id+"F12.opRevolve","SWEPT_BODY",BODY,{"disambiguationData":[OSD([sQuery(id+"F11.wireOp",EDGE,"E8"),sQuery(id+"F11.wireOp",EDGE,"E10")])]}),"instanceName":"1"});
            var Q33;
            Q33=makeQuery(id+"F34.opPattern","COPY",BODY,{"derivedFrom":makeQuery(id+"F20.opExtrude","SWEPT_BODY",BODY,{"disambiguationData":[OSD([sQuery(id+"F19.wireOp",EDGE,"E19")])]}),"instanceName":"1"});
            var Q34;
            Q34=makeQuery(id+"F34.opPattern","COPY",BODY,{"derivedFrom":makeQuery(id+"F24.opExtrude","SWEPT_BODY",BODY,{"disambiguationData":[OSD([sQuery(id+"F23.wireOp",EDGE,"E21")])]}),"instanceName":"1"});
            var Q35;
            Q35=makeQuery(id+"F34.opPattern","COPY",BODY,{"derivedFrom":makeQuery(id+"F25.opPattern","COPY",BODY,{"derivedFrom":makeQuery(id+"F12.opRevolve","SWEPT_BODY",BODY,{"disambiguationData":[OSD([sQuery(id+"F11.wireOp",EDGE,"E8"),sQuery(id+"F11.wireOp",EDGE,"E10")])]}),"instanceName":"1"}),"instanceName":"1"});
            var Q36;
            Q36=makeQuery(id+"F34.opPattern","COPY",BODY,{"derivedFrom":makeQuery(id+"F25.opPattern","COPY",BODY,{"derivedFrom":makeQuery(id+"F20.opExtrude","SWEPT_BODY",BODY,{"disambiguationData":[OSD([sQuery(id+"F19.wireOp",EDGE,"E19")])]}),"instanceName":"1"}),"instanceName":"1"});
            var Q37;
            Q37=makeQuery(id+"F34.opPattern","COPY",BODY,{"derivedFrom":makeQuery(id+"F25.opPattern","COPY",BODY,{"derivedFrom":makeQuery(id+"F24.opExtrude","SWEPT_BODY",BODY,{"disambiguationData":[OSD([sQuery(id+"F23.wireOp",EDGE,"E21")])]}),"instanceName":"1"}),"instanceName":"1"});
            var Q38;
            Q38=makeQuery(id+"F34.opPattern","COPY",BODY,{"derivedFrom":makeQuery(id+"F26.opPattern","COPY",BODY,{"derivedFrom":makeQuery(id+"F12.opRevolve","SWEPT_BODY",BODY,{"disambiguationData":[OSD([sQuery(id+"F11.wireOp",EDGE,"E8"),sQuery(id+"F11.wireOp",EDGE,"E10")])]}),"instanceName":"1"}),"instanceName":"1"});
            var Q39;
            Q39=makeQuery(id+"F34.opPattern","COPY",BODY,{"derivedFrom":makeQuery(id+"F26.opPattern","COPY",BODY,{"derivedFrom":makeQuery(id+"F20.opExtrude","SWEPT_BODY",BODY,{"disambiguationData":[OSD([sQuery(id+"F19.wireOp",EDGE,"E19")])]}),"instanceName":"1"}),"instanceName":"1"});
            var Q40;
            Q40=makeQuery(id+"F34.opPattern","COPY",BODY,{"derivedFrom":makeQuery(id+"F26.opPattern","COPY",BODY,{"derivedFrom":makeQuery(id+"F24.opExtrude","SWEPT_BODY",BODY,{"disambiguationData":[OSD([sQuery(id+"F23.wireOp",EDGE,"E21")])]}),"instanceName":"1"}),"instanceName":"1"});
            var Q41;
            Q41=makeQuery(id+"F34.opPattern","COPY",BODY,{"derivedFrom":makeQuery(id+"F26.opPattern","COPY",BODY,{"derivedFrom":makeQuery(id+"F25.opPattern","COPY",BODY,{"derivedFrom":makeQuery(id+"F20.opExtrude","SWEPT_BODY",BODY,{"disambiguationData":[OSD([sQuery(id+"F19.wireOp",EDGE,"E19")])]}),"instanceName":"1"}),"instanceName":"1"}),"instanceName":"1"});
            var Q42;
            Q42=makeQuery(id+"F34.opPattern","COPY",BODY,{"derivedFrom":makeQuery(id+"F26.opPattern","COPY",BODY,{"derivedFrom":makeQuery(id+"F25.opPattern","COPY",BODY,{"derivedFrom":makeQuery(id+"F24.opExtrude","SWEPT_BODY",BODY,{"disambiguationData":[OSD([sQuery(id+"F23.wireOp",EDGE,"E21")])]}),"instanceName":"1"}),"instanceName":"1"}),"instanceName":"1"});
            var Q43;
            Q43=makeQuery(id+"F34.opPattern","COPY",BODY,{"derivedFrom":makeQuery(id+"F28.opExtrude","SWEPT_BODY",BODY,{"disambiguationData":[OSD([sQuery(id+"F27.wireOp",EDGE,"E23")])]}),"instanceName":"1"});
            var Q44;
            Q44=makeQuery(id+"F34.opPattern","COPY",BODY,{"derivedFrom":makeQuery(id+"F29.opPattern","COPY",BODY,{"derivedFrom":makeQuery(id+"F28.opExtrude","SWEPT_BODY",BODY,{"disambiguationData":[OSD([sQuery(id+"F27.wireOp",EDGE,"E23")])]}),"instanceName":"1"}),"instanceName":"1"});
            var Q45;
            Q45=makeQuery(id+"F32.opPattern","COPY",BODY,{"derivedFrom":makeQuery(id+"F9.opRevolve","SWEPT_BODY",BODY,{"disambiguationData":[OSD([sQuery(id+"F8.wireOp",EDGE,"E4"),sQuery(id+"F8.wireOp",EDGE,"E6")])]}),"instanceName":"1"});
            var Q46;
            Q46=makeQuery(id+"F26.opPattern","COPY",BODY,{"derivedFrom":makeQuery(id+"F9.opRevolve","SWEPT_BODY",BODY,{"disambiguationData":[OSD([sQuery(id+"F8.wireOp",EDGE,"E4"),sQuery(id+"F8.wireOp",EDGE,"E6")])]}),"instanceName":"1"});
            var Q47;
            Q47=makeQuery(id+"F26.opPattern","COPY",BODY,{"derivedFrom":makeQuery(id+"F10.opRevolve","SWEPT_BODY",BODY,{"disambiguationData":[OSD([sQuery(id+"F8.wireOp",EDGE,"E5"),sQuery(id+"F8.wireOp",EDGE,"E7")])]}),"instanceName":"1"});
            var Q48;
            Q48=makeQuery(id+"F32.opPattern","COPY",BODY,{"derivedFrom":makeQuery(id+"F12.opRevolve","SWEPT_BODY",BODY,{"disambiguationData":[OSD([sQuery(id+"F11.wireOp",EDGE,"E8"),sQuery(id+"F11.wireOp",EDGE,"E10")])]}),"instanceName":"1"});
            var Q49;
            Q49=makeQuery(id+"F32.opPattern","COPY",BODY,{"derivedFrom":makeQuery(id+"F26.opPattern","COPY",BODY,{"derivedFrom":makeQuery(id+"F9.opRevolve","SWEPT_BODY",BODY,{"disambiguationData":[OSD([sQuery(id+"F8.wireOp",EDGE,"E4"),sQuery(id+"F8.wireOp",EDGE,"E6")])]}),"instanceName":"1"}),"instanceName":"1"});
            var Q50;
            Q50=makeQuery(id+"F34.opPattern","COPY",BODY,{"derivedFrom":makeQuery(id+"F9.opRevolve","SWEPT_BODY",BODY,{"disambiguationData":[OSD([sQuery(id+"F8.wireOp",EDGE,"E4"),sQuery(id+"F8.wireOp",EDGE,"E6")])]}),"instanceName":"1"});
            var Q51;
            Q51=makeQuery(id+"F34.opPattern","COPY",BODY,{"derivedFrom":makeQuery(id+"F26.opPattern","COPY",BODY,{"derivedFrom":makeQuery(id+"F9.opRevolve","SWEPT_BODY",BODY,{"disambiguationData":[OSD([sQuery(id+"F8.wireOp",EDGE,"E4"),sQuery(id+"F8.wireOp",EDGE,"E6")])]}),"instanceName":"1"}),"instanceName":"1"});
            var Q52;
            Q52=makeQuery(id+"F34.opPattern","COPY",BODY,{"derivedFrom":makeQuery(id+"F26.opPattern","COPY",BODY,{"derivedFrom":makeQuery(id+"F10.opRevolve","SWEPT_BODY",BODY,{"disambiguationData":[OSD([sQuery(id+"F8.wireOp",EDGE,"E5"),sQuery(id+"F8.wireOp",EDGE,"E7")])]}),"instanceName":"1"}),"instanceName":"1"});
            var Q53;
            Q53=makeQuery(id+"F34.opPattern","COPY",BODY,{"derivedFrom":makeQuery(id+"F26.opPattern","COPY",BODY,{"derivedFrom":makeQuery(id+"F25.opPattern","COPY",BODY,{"derivedFrom":makeQuery(id+"F12.opRevolve","SWEPT_BODY",BODY,{"disambiguationData":[OSD([sQuery(id+"F11.wireOp",EDGE,"E8"),sQuery(id+"F11.wireOp",EDGE,"E10")])]}),"instanceName":"1"}),"instanceName":"1"}),"instanceName":"1"});
            var Q54;
            Q54=sQuery(id+"F2.wireOp",EDGE,"E1");
            transform(context, id + "F36", {"entities" : qUnion([Q0, Q1, Q2, Q3, Q4, Q5, Q6, Q7, Q8, Q9, Q10, Q11, Q12, Q13, Q14, Q15, Q16, Q17, Q18, Q19, Q20, Q21, Q22, Q23, Q24, Q25, Q26, Q27, Q28, Q29, Q30, Q31, Q32, Q33, Q34, Q35, Q36, Q37, Q38, Q39, Q40, Q41, Q42, Q43, Q44, Q45, Q46, Q47, Q48, Q49, Q50, Q51, Q52, Q53]), "transformType" : TransformType.ROTATION, "transformAxis" : qUnion([Q54]), "angle" : 20.9 * degree, "makeCopy" : false});
        }
        {
            var Q0;
            Q0=makeQuery(id+"F10.opRevolve","SWEPT_BODY",BODY,{"disambiguationData":[OSD([sQuery(id+"F8.wireOp",EDGE,"E5"),sQuery(id+"F8.wireOp",EDGE,"E7")])]});
            deleteBodies(context, id + "F37", {"entities" : qUnion([Q0])});
        }
        {
            var Q0;
            Q0=makeQuery(id+"F34.opPattern","COPY",BODY,{"derivedFrom":makeQuery(id+"F26.opPattern","COPY",BODY,{"derivedFrom":makeQuery(id+"F10.opRevolve","SWEPT_BODY",BODY,{"disambiguationData":[OSD([sQuery(id+"F8.wireOp",EDGE,"E5"),sQuery(id+"F8.wireOp",EDGE,"E7")])]}),"instanceName":"1"}),"instanceName":"1"});
            deleteBodies(context, id + "F38", {"entities" : qUnion([Q0])});
        }
        {
            var Q0;
            Q0=makeQuery(id+"F32.opPattern","COPY",BODY,{"derivedFrom":makeQuery(id+"F25.opPattern","COPY",BODY,{"derivedFrom":makeQuery(id+"F12.opRevolve","SWEPT_BODY",BODY,{"disambiguationData":[OSD([sQuery(id+"F11.wireOp",EDGE,"E8"),sQuery(id+"F11.wireOp",EDGE,"E10")])]}),"instanceName":"1"}),"instanceName":"1"});
            deleteBodies(context, id + "F39", {"entities" : qUnion([Q0])});
        }
        {
            var Q0;
            Q0=makeQuery(id+"F6.opPattern","COPY",BODY,{"derivedFrom":makeQuery(id+"F1.opExtrude","SWEPT_BODY",BODY,{"disambiguationData":[OSD([sQuery(id+"F0.wireOp",EDGE,"E0.bottom"),sQuery(id+"F0.wireOp",EDGE,"E0.top"),sQuery(id+"F0.wireOp",EDGE,"E0.left"),sQuery(id+"F0.wireOp",EDGE,"E0.right")])]}),"instanceName":"1"});
            deleteBodies(context, id + "F40", {"entities" : qUnion([Q0])});
        }
        {
            var Q0;
            Q0=makeQuery(id+"F34.opPattern","COPY",BODY,{"derivedFrom":makeQuery(id+"F6.opPattern","COPY",BODY,{"derivedFrom":makeQuery(id+"F1.opExtrude","SWEPT_BODY",BODY,{"disambiguationData":[OSD([sQuery(id+"F0.wireOp",EDGE,"E0.bottom"),sQuery(id+"F0.wireOp",EDGE,"E0.top"),sQuery(id+"F0.wireOp",EDGE,"E0.left"),sQuery(id+"F0.wireOp",EDGE,"E0.right")])]}),"instanceName":"1"}),"instanceName":"1"});
            deleteBodies(context, id + "F41", {"entities" : qUnion([Q0])});
        }
        {
            var Q0;
            Q0=makeQuery(id+"F32.opPattern","COPY",BODY,{"derivedFrom":makeQuery(id+"F6.opPattern","COPY",BODY,{"derivedFrom":makeQuery(id+"F1.opExtrude","SWEPT_BODY",BODY,{"disambiguationData":[OSD([sQuery(id+"F0.wireOp",EDGE,"E0.bottom"),sQuery(id+"F0.wireOp",EDGE,"E0.top"),sQuery(id+"F0.wireOp",EDGE,"E0.left"),sQuery(id+"F0.wireOp",EDGE,"E0.right")])]}),"instanceName":"1"}),"instanceName":"1"});
            deleteBodies(context, id + "F42", {"entities" : qUnion([Q0])});
        }
        {
            var Q0;
            Q0=makeQuery(id+"F32.opPattern","COPY",BODY,{"derivedFrom":makeQuery(id+"F9.opRevolve","SWEPT_BODY",BODY,{"disambiguationData":[OSD([sQuery(id+"F8.wireOp",EDGE,"E4"),sQuery(id+"F8.wireOp",EDGE,"E6")])]}),"instanceName":"1"});
            var Q1;
            Q1=makeQuery(id+"F9.opRevolve","SWEPT_BODY",BODY,{"disambiguationData":[OSD([sQuery(id+"F8.wireOp",EDGE,"E4"),sQuery(id+"F8.wireOp",EDGE,"E6")])]});
            booleanBodies(context, id + "F43", {"operationType" : BooleanOperationType.SUBTRACTION, "tools" : qUnion([Q0]), "targets" : qUnion([Q1]), "keepTools" : true});
        }
    });
